# Revit family: KS ALU-PU 80 -s-, DS 20, M 8-M10, Ø 60,3- 88,9
name_source: partatom
category: HLS-Bauteile
units: mm (PartAtom-declared; Revit-internal decimal feet)

## family parameters
Arbeitsebenenbasiert = Ja
Beim Laden mit Abzugskörper schneiden = Nein
Bemaßung runder Anschluss = Durchmesser verwenden
Beschriftungsausrichtung beibehalten = Nein
Gemeinsam genutzt = Ja
Immer vertikal = Nein
Raumberechnungspunkt = Nein
Teiletyp = Normal

## types (5) — shared parameters
A = 40 mm  [stored 0.131234 ft]
Anschluss = M8/M10
BP = 14 mm  [stored 0.0459318 ft]
Baustoffklasse = B2
DS = 20 mm  [stored 0.0656168 ft]
DVS = 5 mm  [stored 0.0164042 ft]
Dichte Kern = 80 kg/m³
Dichte Mantel = 2700 kg/m³
Dicke Mantel = 0.08 mm
Dämmkörper = ALU/PU
Dämmstärke = 20 mm  [stored 0.0656168 ft]
Fabrikat = MEFA
Firma = MEFA Befestigungs- und Montagesysteme GmbH
HGA = 17 mm
Kurztext1 = Kälteschelle RG80s ALU/PU
L Ü Bogen = 19 mm  [stored 0.062336 ft]
MB = 25 mm  [stored 0.082021 ft]
MD = 3 mm  [stored 0.00984252 ft]
Material = Stahl
Material Mantel = Alufolie
Materialname = DD11
Mengeneinheit = St
Oberflaeche = galvanisch verzinkt
Vorgabe-Ansicht = 1219 mm
Wasserdampfdiffusionswiderstand = 18750 µ
Wärmeleitfähigkeit = 0.025 W/mK
d1 = 7 mm  [stored 0.0229659 ft]
max. Temperaturbeständigkeit = 120 °C
mittl. Nenndruckfestigkeit Kern = 0.5 N/mm²
stat. Belastung Kern = 0.1 N/mm²
vpe = 1

## per-type parameters (varying)
- Kälteschelle ALU-PU 80 -s-, DS 20, M8/M10, Ø 60,3: AB=0 mm  [stored 0 ft]; Anschlußhöhe=39 mm; Artikelnummer=70506049; B=136 mm; Breite=136 mm; D=60 mm  [stored 0.19685 ft]; D0=100 mm  [stored 0.328084 ft]; DF1=14 mm  [stored 0.0459318 ft]; DF2=15 mm  [stored 0.0492126 ft]; Dmax=62 mm  [stored 0.203412 ft]; Dmin=60 mm  [stored 0.19685 ft]; EAN=4250928441317; Gewicht=0.24 kg; Gewicht pro Bauteil=0.24 kg; H=122 mm; Kurztext2=60,3 mm Iso 20 x 50 mm M8/M10; L=50 mm  [stored 0.164042 ft]; R=50 mm  [stored 0.164042 ft]; RM=53 mm; Rohraußendurchmesser Stahl=60,3 mm; Rohrschellentyp=Trabant; S=122 mm; S1=119 mm; Schalenlänge=50 mm; max. zul. Last=0.40 kN
- Kälteschelle ALU-PU 80 -s-, DS 20, M8/M10, Ø 63,5: AB=2 mm  [stored 0.00656168 ft]; Anschlußhöhe=41 mm; Artikelnummer=70506449; B=144 mm; Breite=143 mm; D=64 mm  [stored 0.209974 ft]; D0=104 mm; DF1=17 mm; DF2=18 mm  [stored 0.0590551 ft]; Dmax=64 mm  [stored 0.209974 ft]; Dmin=62 mm  [stored 0.203412 ft]; EAN=4250928441324; Gewicht=0.25 kg; Gewicht pro Bauteil=0.25 kg; H=126 mm; Kurztext2=63,5 mm Iso 20 x 50 mm M8/M10; L=50 mm  [stored 0.164042 ft]; R=52 mm; RM=54 mm; Rohraußendurchmesser Stahl=63,5 mm; Rohrschellentyp=Omnia MB; S=127 mm; S1=123 mm; Schalenlänge=50 mm; max. zul. Last=0.40 kN
- Kälteschelle ALU-PU 80 -s-, DS 20, M8/M10, Ø 70: AB=2 mm  [stored 0.00656168 ft]; Anschlußhöhe=39 mm; Artikelnummer=70607049; B=144 mm; Breite=152 mm; D=70 mm  [stored 0.229659 ft]; D0=110 mm; DF1=13 mm; DF2=14 mm  [stored 0.0459318 ft]; Dmax=72 mm  [stored 0.23622 ft]; Dmin=68 mm  [stored 0.223097 ft]; EAN=4250928441331; Gewicht=0.25 kg; Gewicht pro Bauteil=0.25 kg; H=132 mm; Kurztext2=70 mm Iso 20 x 66 mm M8/M10; L=66 mm  [stored 0.216535 ft]; R=55 mm  [stored 0.180446 ft]; RM=58 mm  [stored 0.190289 ft]; Rohraußendurchmesser Stahl=70 mm; Rohrschellentyp=Omnia MB; S=131 mm; S1=129 mm; Schalenlänge=66 mm; max. zul. Last=0.40 kN
- Kälteschelle ALU-PU 80 -s-, DS 20, M8/M10, Ø 76,1: AB=2 mm  [stored 0.00656168 ft]; Anschlußhöhe=42 mm; Artikelnummer=70607649; B=158 mm; Breite=158 mm; D=76 mm  [stored 0.249344 ft]; D0=116 mm; DF1=17 mm; DF2=18 mm  [stored 0.0590551 ft]; Dmax=78 mm  [stored 0.255906 ft]; Dmin=74 mm  [stored 0.242782 ft]; EAN=4250928441355; Gewicht=0.28 kg; Gewicht pro Bauteil=0.28 kg; H=138 mm; Kurztext2=76,1 mm Iso 20 x 66 mm M8/M10; L=66 mm  [stored 0.216535 ft]; R=58 mm  [stored 0.190289 ft]; RM=61 mm  [stored 0.200131 ft]; Rohraußendurchmesser Stahl=76,1 mm; Rohrschellentyp=Omnia MB; S=141 mm; S1=135 mm; Schalenlänge=66 mm; max. zul. Last=0.40 kN
- Kälteschelle ALU-PU 80 -s-, DS 20, M8/M10, Ø 88,9: AB=1 mm  [stored 0.00328084 ft]; Anschlußhöhe=42 mm; Artikelnummer=75208949; B=177 mm; Breite=175 mm; D=89 mm; D0=129 mm; DF1=21 mm  [stored 0.0688976 ft]; DF2=21 mm  [stored 0.0688976 ft]; Dmax=90 mm  [stored 0.295276 ft]; Dmin=88 mm  [stored 0.288714 ft]; EAN=4250928443083; Gewicht=0.32 kg; Gewicht pro Bauteil=0.32 kg; H=151 mm; Kurztext2=88,9 mm Iso 20 x 83 mm M8/M10; L=83 mm  [stored 0.27231 ft]; R=64 mm  [stored 0.209974 ft]; RM=67 mm; Rohraußendurchmesser Stahl=88,9 mm; Rohrschellentyp=Omnia MB; S=156 mm; S1=148 mm; Schalenlänge=83 mm; max. zul. Last=0.50 kN

note: [stored X ft] marks values corroborated as IEEE doubles in the binary element streams (Revit-internal decimal feet)

## geometry (parser evidence)
native form markers: Sweep x2
no freeform markers — native parametric forms only
